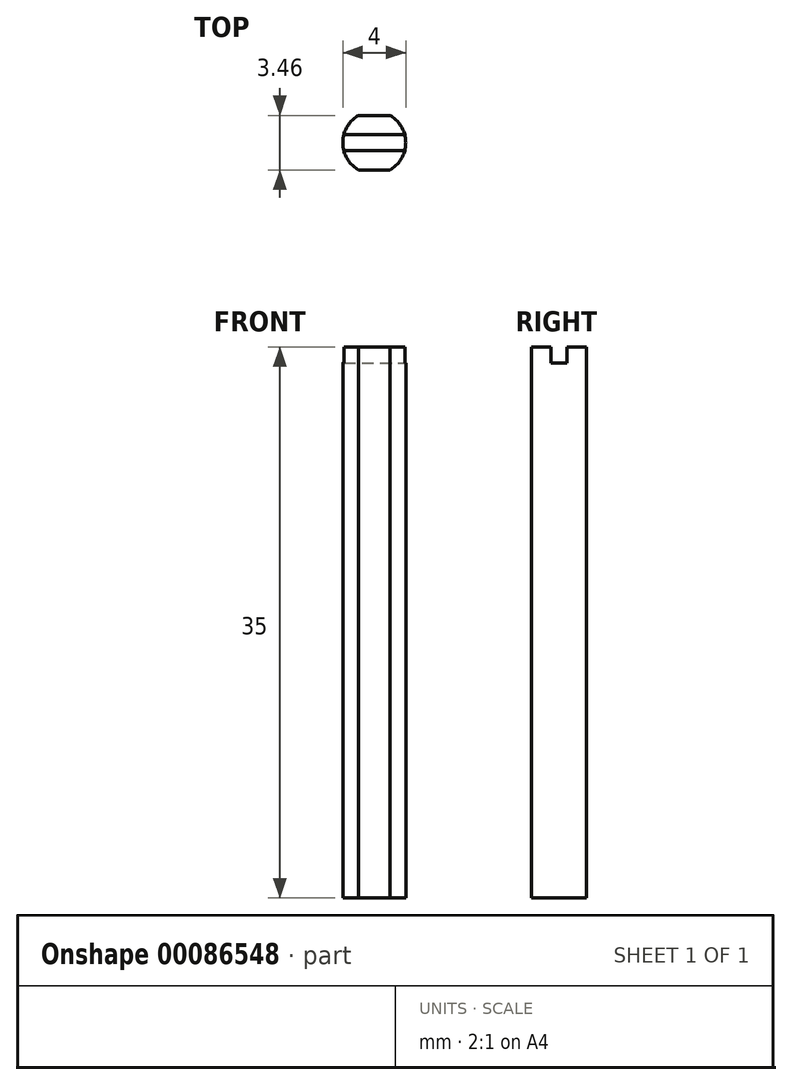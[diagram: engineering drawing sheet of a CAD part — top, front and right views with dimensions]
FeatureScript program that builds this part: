
annotation { "Feature Type Name" : "Feature", "Feature Type Description" : "" }
export const myFeature = defineFeature(function(context is Context, id is Id, definition is map)
    precondition{}
    {
        {
            var Q0;
            Q0=qCreatedBy(makeId("Top.planeOp"),FACE);
            var sketch = newSketch(context, id + "F0", { "sketchPlane" : qUnion([Q0])});
            skArc(sketch, "E0", {"start": v(1, -1.73) * mm, "mid": v(2, 0) * mm, "end": v(1, 1.73) * mm});
            skLineSegment(sketch, "E1", {"start": v(-1, -1.73) * mm, "end": v(1, -1.73) * mm});
            skLineSegment(sketch, "E2", {"start": v(0, 0) * mm, "end": v(0, -1.73) * mm, "construction": true});
            skLineSegment(sketch, "E3", {"start": v(-1, 1.73) * mm, "end": v(1, 1.73) * mm});
            skArc(sketch, "E4.trimOffspring", {"start": v(-1, 1.73) * mm, "mid": v(-2, 0) * mm, "end": v(-1, -1.73) * mm});
            skSolve(sketch);
        }
        {
            var Q0;
            Q0 = qSketchRegion(id + "F0", true);
            extrude(context, id + "F1", {"entities" : qUnion([Q0]), "depth" : 35 * mm});
        }
        {
            var Q0;
            Q0=makeQuery(id+"F1.opExtrude","CAP_FACE",FACE,{"disambiguationData":[OSD([sQuery(id+"F0.wireOp",EDGE,"E0"),sQuery(id+"F0.wireOp",EDGE,"E1"),sQuery(id+"F0.wireOp",EDGE,"E3"),sQuery(id+"F0.wireOp",EDGE,"E4.trimOffspring")])],"isStart":false});
            var sketch = newSketch(context, id + "F2", { "sketchPlane" : qUnion([Q0])});
            skPoint(sketch, "E5", {"position": v(0, 0) * mm});
            skLineSegment(sketch, "E6.bottom", {"start": v(-5, 0.5) * mm, "end": v(5, 0.5) * mm});
            skLineSegment(sketch, "E6.top", {"start": v(-5, -0.5) * mm, "end": v(5, -0.5) * mm});
            skLineSegment(sketch, "E6.left", {"start": v(-5, 0.5) * mm, "end": v(-5, -0.5) * mm});
            skLineSegment(sketch, "E6.right", {"start": v(5, 0.5) * mm, "end": v(5, -0.5) * mm});
            skSolve(sketch);
        }
        {
            var Q0;
            Q0 = qSketchRegion(id + "F2", true);
            extrude(context, id + "F3", {"entities" : qUnion([Q0]), "operationType" : NewBodyOperationType.REMOVE, "oppositeDirection" : true, "depth" : 1 * mm});
        }
    });
